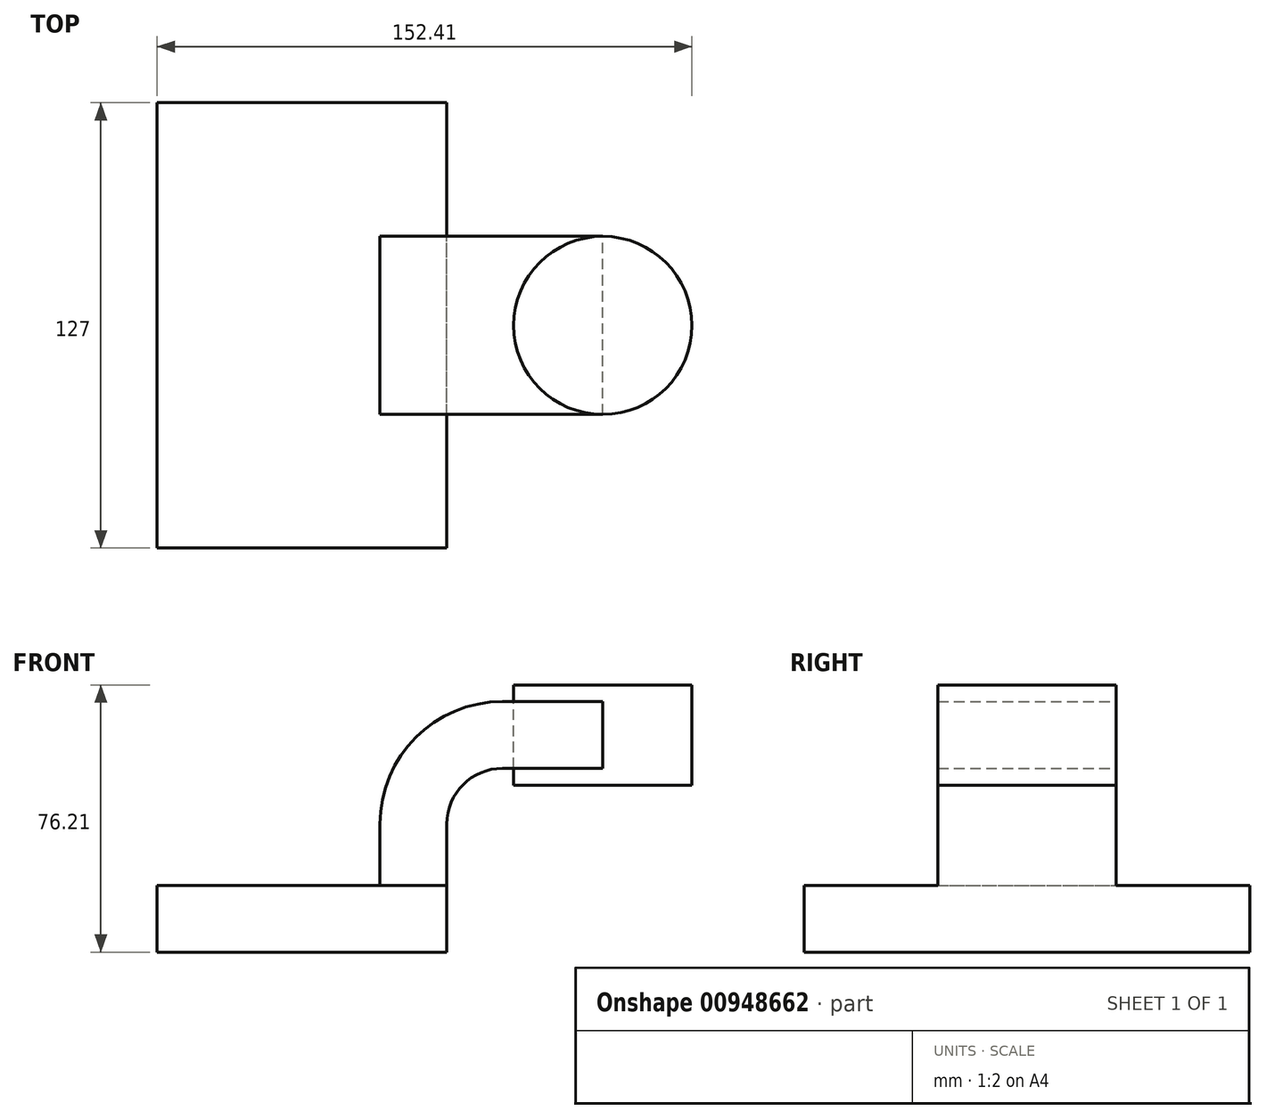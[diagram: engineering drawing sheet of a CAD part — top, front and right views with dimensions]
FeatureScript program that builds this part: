
annotation { "Feature Type Name" : "Feature", "Feature Type Description" : "" }
export const myFeature = defineFeature(function(context is Context, id is Id, definition is map)
    precondition{}
    {
        {
            var Q0;
            Q0=qCreatedBy(makeId("Front.planeOp"),FACE);
            var sketch = newSketch(context, id + "F0", { "sketchPlane" : qUnion([Q0])});
            skLineSegment(sketch, "E0.bottom", {"start": v(-41.28, 9.52) * mm, "end": v(41.28, 9.52) * mm});
            skLineSegment(sketch, "E0.top", {"start": v(-41.27, -9.53) * mm, "end": v(41.28, -9.52) * mm});
            skLineSegment(sketch, "E0.left", {"start": v(-41.28, 9.52) * mm, "end": v(-41.27, -9.53) * mm});
            skLineSegment(sketch, "E0.right", {"start": v(41.27, 9.52) * mm, "end": v(41.28, -9.53) * mm});
            skPoint(sketch, "E0.middle", {"position": v(0, 0) * mm});
            skLineSegment(sketch, "E1.bottom", {"start": v(60.32, 66.67) * mm, "end": v(111.12, 66.67) * mm});
            skLineSegment(sketch, "E1.top", {"start": v(60.32, 38.1) * mm, "end": v(111.12, 38.1) * mm});
            skLineSegment(sketch, "E1.left", {"start": v(60.32, 66.67) * mm, "end": v(60.32, 38.1) * mm});
            skLineSegment(sketch, "E1.right", {"start": v(111.12, 66.68) * mm, "end": v(111.12, 38.1) * mm});
            skPoint(sketch, "E1.middle", {"position": v(85.72, 52.39) * mm});
            skLineSegment(sketch, "E2", {"start": v(41.27, 9.52) * mm, "end": v(41.27, 27) * mm});
            skArc(sketch, "E3", {"start": v(41.27, 27) * mm, "mid": v(45.92, 38.23) * mm, "end": v(57.15, 42.88) * mm});
            skLineSegment(sketch, "E4", {"start": v(57.15, 42.88) * mm, "end": v(85.72, 42.88) * mm});
            skLineSegment(sketch, "E5.0", {"start": v(57.15, 61.93) * mm, "end": v(85.72, 61.93) * mm});
            skArc(sketch, "E5.1", {"start": v(22.22, 27) * mm, "mid": v(32.45, 51.7) * mm, "end": v(57.15, 61.93) * mm});
            skLineSegment(sketch, "E5.2", {"start": v(22.22, 9.53) * mm, "end": v(22.22, 27) * mm});
            skFitSpline(sketch, "E6", {"points": [v(-41.28, 9.52) * mm, v(57.15, 61.93) * mm], "startDerivative": vector(6.25, 64.38) * mm, "endDerivative": vector(120.49, -0.13) * mm});
            skLineSegment(sketch, "E7", {"start": v(85.72, 38.1) * mm, "end": v(85.72, 42.88) * mm});
            skLineSegment(sketch, "E8", {"start": v(85.72, 61.93) * mm, "end": v(85.72, 42.88) * mm});
            skLineSegment(sketch, "E9", {"start": v(85.72, 61.93) * mm, "end": v(85.72, 66.67) * mm});
            skSolve(sketch);
        }
        {
            var Q0;
            Q0=makeQuery(id+"F0.imprint","IMPRINT",FACE,{"disambiguationData":[TD([[makeQuery(id+"F0.imprint","IMPRINT",EDGE,{"derivedFrom":sQuery(id+"F0.wireOp",EDGE,"E0.top")}),1.0]])]});
            extrude(context, id + "F1", {"entities" : qUnion([Q0]), "endBound" : BoundingType.SYMMETRIC, "depth" : 127 * mm, "offsetDistance" : 25.4 * mm});
        }
        {
            var Q0;
            {var subQ1=sQuery(id+"F0.wireOp",EDGE,"E2");Q0=makeQuery(id+"F0.imprint","IMPRINT",FACE,{"disambiguationData":[TD([[makeQuery(id+"F0.imprint","IMPRINT",EDGE,{"derivedFrom":subQ1}),1.0]])]});}
            var Q1;
            {var subQ5=sQuery(id+"F0.wireOp",EDGE,"E8");Q1=makeQuery(id+"F0.imprint","IMPRINT",FACE,{"disambiguationData":[TD([[makeQuery(id+"F0.imprint","IMPRINT",EDGE,{"derivedFrom":subQ5}),-1.0]])]});}
            extrude(context, id + "F2", {"entities" : qUnion([Q0, Q1]), "operationType" : NewBodyOperationType.ADD, "endBound" : BoundingType.SYMMETRIC, "depth" : 50.8 * mm, "offsetDistance" : 25.4 * mm});
        }
        {
            var Q0;
            Q0=makeQuery(id+"F0.imprint","IMPRINT",FACE,{"disambiguationData":[TD([[makeQuery(id+"F0.imprint","IMPRINT",EDGE,{"derivedFrom":sQuery(id+"F0.wireOp",EDGE,"E5.1")}),1.0]])]});
            extrude(context, id + "F3", {"entities" : qUnion([Q0]), "operationType" : NewBodyOperationType.ADD, "endBound" : BoundingType.SYMMETRIC, "depth" : 15.88 * mm, "offsetDistance" : 25.4 * mm});
        }
        {
            var Q0;
            {var subQ1=sQuery(id+"F0.wireOp",EDGE,"E1.right");Q0=makeQuery(id+"F0.imprint","IMPRINT",FACE,{"disambiguationData":[TD([[makeQuery(id+"F0.imprint","IMPRINT",EDGE,{"derivedFrom":subQ1}),-1.0]])]});}
            var Q1;
            Q1=sQuery(id+"F0.wireOp",EDGE,"E8");
            revolve(context, id + "F4", {"surfaceOperationType" : NewSurfaceOperationType.NEW, "entities" : qUnion([Q0]), "axis" : qUnion([Q1]), "revolveType" : RevolveType.FULL});
        }
    });
